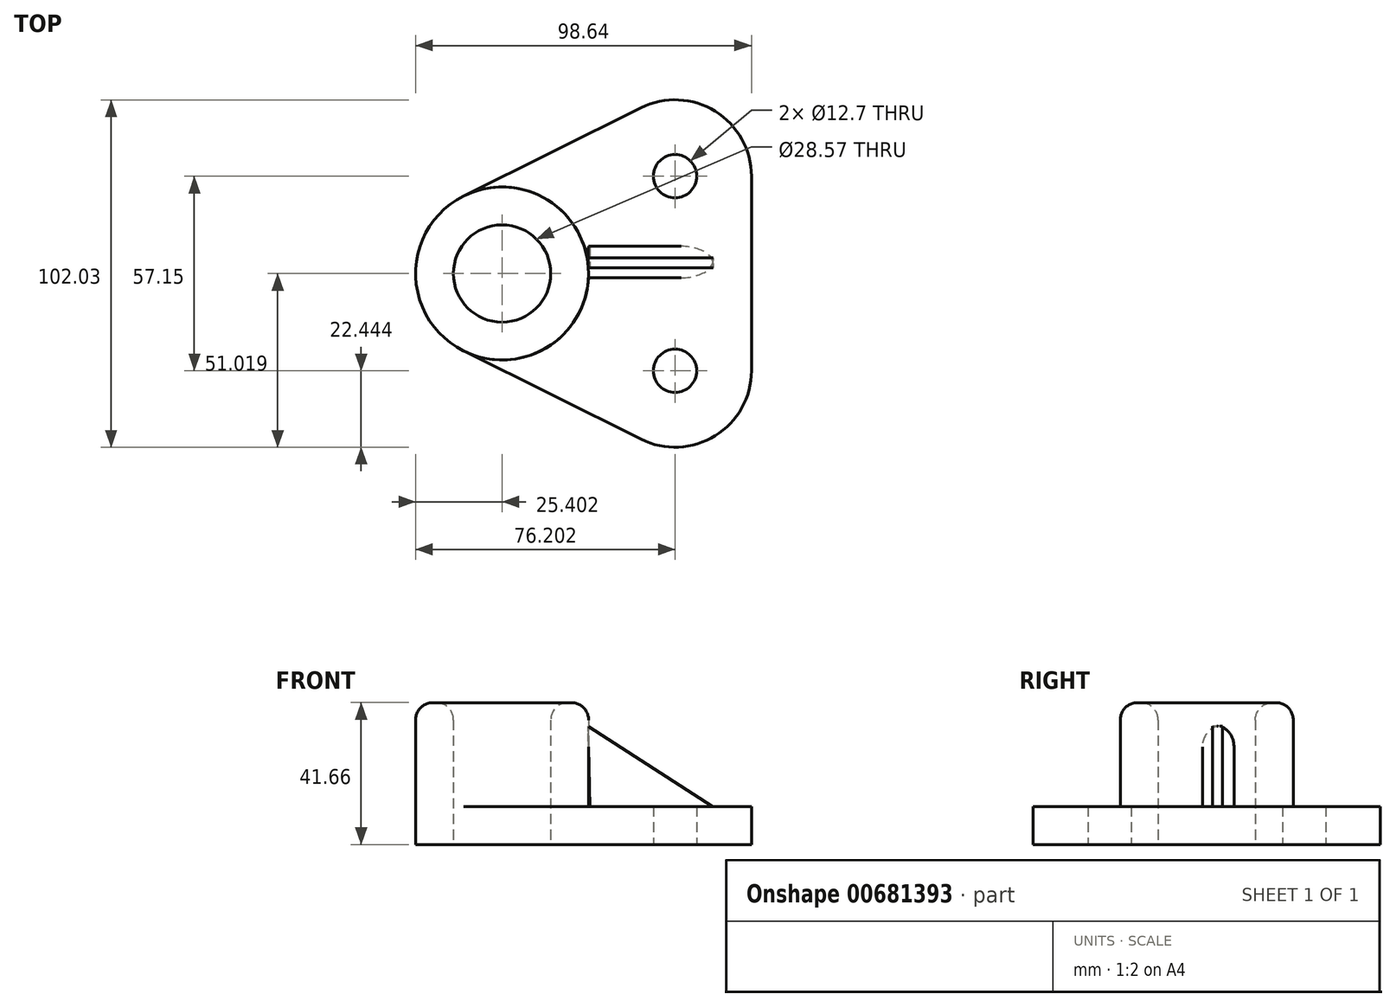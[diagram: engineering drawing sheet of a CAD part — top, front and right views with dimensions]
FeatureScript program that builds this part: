
annotation { "Feature Type Name" : "Feature", "Feature Type Description" : "" }
export const myFeature = defineFeature(function(context is Context, id is Id, definition is map)
    precondition{}
    {
        {
            var Q0;
            Q0=qCreatedBy(makeId("Top.planeOp"),FACE);
            var sketch = newSketch(context, id + "F0", { "sketchPlane" : qUnion([Q0])});
            skCircle(sketch, "E0", {"center": v(9.41, 57.15) * mm, "radius": 6.35 * mm});
            skCircle(sketch, "E1", {"center": v(9.41, 0) * mm, "radius": 6.35 * mm});
            skCircle(sketch, "E2", {"center": v(-41.39, 28.58) * mm, "radius": 14.29 * mm});
            skCircle(sketch, "E3", {"center": v(-41.39, 28.58) * mm, "radius": 25.4 * mm});
            skArc(sketch, "E4", {"start": v(31.85, 57.15) * mm, "mid": v(21.23, 76.23) * mm, "end": v(-0.58, 77.24) * mm});
            skArc(sketch, "E5", {"start": v(-0.58, -20.1) * mm, "mid": v(21.23, -19.08) * mm, "end": v(31.85, 0) * mm});
            skLineSegment(sketch, "E6", {"start": v(-52.7, 51.32) * mm, "end": v(-0.58, 77.24) * mm});
            skLineSegment(sketch, "E7", {"start": v(31.85, 57.15) * mm, "end": v(31.85, 0) * mm});
            skLineSegment(sketch, "E8", {"start": v(-52.7, 5.83) * mm, "end": v(0, -20.38) * mm});
            skLineSegment(sketch, "E9.bottom", {"start": v(-15.99, 40.05) * mm, "end": v(29.43, 40.05) * mm});
            skLineSegment(sketch, "E9.top", {"start": v(-15.99, 18.56) * mm, "end": v(29.43, 18.56) * mm});
            skLineSegment(sketch, "E9.left", {"start": v(-15.99, 40.05) * mm, "end": v(-15.99, 18.56) * mm});
            skLineSegment(sketch, "E9.right", {"start": v(29.43, 40.05) * mm, "end": v(29.43, 18.56) * mm});
            skSolve(sketch);
        }
        {
            var Q0;
            Q0=makeQuery(id+"F0.imprint","IMPRINT",FACE,{"disambiguationData":[TD([[makeQuery(id+"F0.imprint","IMPRINT",EDGE,{"derivedFrom":sQuery(id+"F0.wireOp",EDGE,"E2")}),-1.0]])]});
            extrude(context, id + "F1", {"entities" : qUnion([Q0]), "depth" : 41.66 * mm, "offsetDistance" : 25.4 * mm});
        }
        {
            var Q0;
            Q0=makeQuery(id+"F0.imprint","IMPRINT",FACE,{"disambiguationData":[TD([[makeQuery(id+"F0.imprint","IMPRINT",EDGE,{"derivedFrom":sQuery(id+"F0.wireOp",EDGE,"E0")}),-1.0]])]});
            var Q1;
            {var subQ3=sQuery(id+"F0.wireOp",EDGE,"E9.bottom");Q1=makeQuery(id+"F0.imprint","IMPRINT",FACE,{"disambiguationData":[TD([[makeQuery(id+"F0.imprint","IMPRINT",EDGE,{"derivedFrom":subQ3}),-1.0]])]});}
            extrude(context, id + "F2", {"entities" : qUnion([Q0, Q1]), "operationType" : NewBodyOperationType.ADD, "depth" : 11.18 * mm, "offsetDistance" : 25.4 * mm});
        }
        {
            var Q0;
            Q0=qCreatedBy(makeId("Front.planeOp"),FACE);
            var sketch = newSketch(context, id + "F3", { "sketchPlane" : qUnion([Q0])});
            skLineSegment(sketch, "E10", {"start": v(-16.13, 34.75) * mm, "end": v(20.56, 11.15) * mm});
            skLineSegment(sketch, "E11", {"start": v(20.56, 11.15) * mm, "end": v(-15.58, 11.15) * mm});
            skLineSegment(sketch, "E12", {"start": v(-15.58, 11.15) * mm, "end": v(-16.13, 34.75) * mm});
            skSolve(sketch);
        }
        {
            var Q0;
            Q0=qSketchRegion(id+"F3",true);
            extrude(context, id + "F4", {"entities" : qUnion([Q0]), "oppositeDirection" : true, "depth" : 5.84 * mm, "offsetDistance" : 25.4 * mm, "symmetric" : true});
        }
        {
            var Q0;
            Q0=makeQuery(id+"F1.opExtrude","SWEPT_BODY",BODY,{"disambiguationData":[OSD([sQuery(id+"F0.wireOp",EDGE,"E2"),sQuery(id+"F0.wireOp",EDGE,"E3")])]});
            transform(context, id + "F5", {"entities" : qUnion([Q0]), "transformType" : TransformType.TRANSLATION_3D, "dx" : 0 * mm, "dy" : -30.23 * mm, "dz" : 0 * mm, "makeCopy" : false});
        }
        {
            var Q0;
            Q0=qSketchRegion(id+"F3",true);
            extrude(context, id + "F6", {"entities" : qUnion([Q0]), "oppositeDirection" : true, "depth" : 6.35 * mm, "offsetDistance" : 25.4 * mm});
        }
        {
            var Q0;
            Q0=makeQuery(id+"F1.opExtrude","CAP_FACE",FACE,{"disambiguationData":[OSD([sQuery(id+"F0.wireOp",EDGE,"E2"),sQuery(id+"F0.wireOp",EDGE,"E3")])],"isStart":false});
            var Q1;
            Q1=makeQuery(id+"F4.opExtrude","CAP_EDGE",EDGE,{"disambiguationData":[OSD([sQuery(id+"F3.wireOp",EDGE,"E10")])],"isStart":true});
            var Q2;
            Q2=makeQuery(id+"F6.opExtrude","CAP_EDGE",EDGE,{"disambiguationData":[OSD([sQuery(id+"F3.wireOp",EDGE,"E10")])],"isStart":false});
            var Q3;
            Q3=makeQuery(id+"F2.opExtrude","CAP_EDGE",EDGE,{"disambiguationData":[OSD([sQuery(id+"F0.wireOp",EDGE,"E3")])],"isStart":false});
            fillet(context, id + "F7", {"entities" : qUnion([Q0, Q1, Q2, Q3]), "radius" : 5.08 * mm, "tangentPropagation" : true, "allowEdgeOverflow" : false});
        }
    });
